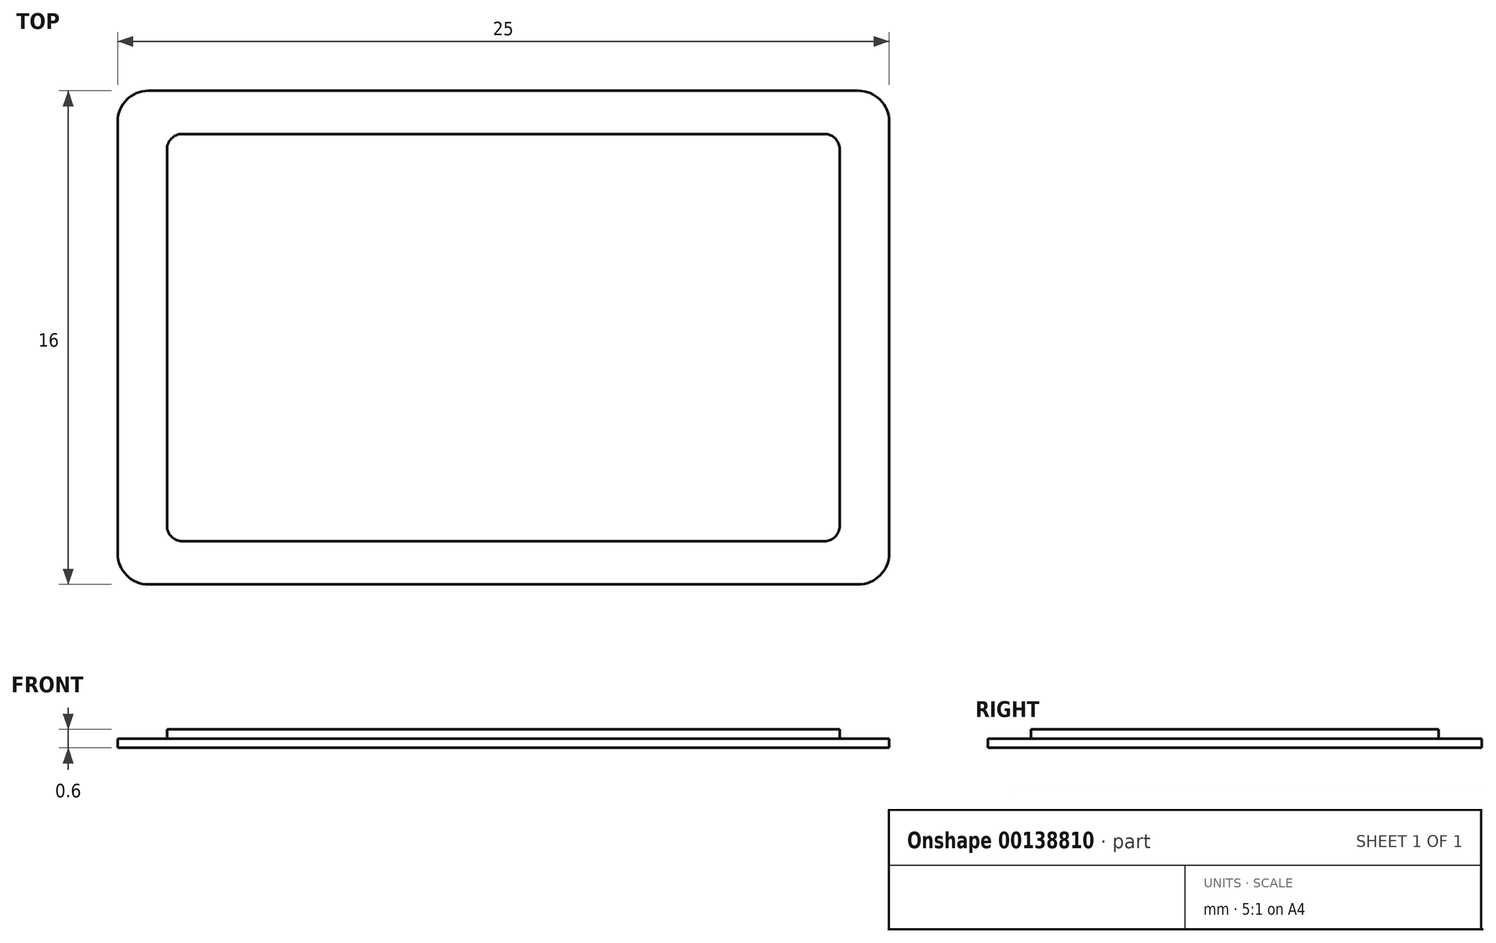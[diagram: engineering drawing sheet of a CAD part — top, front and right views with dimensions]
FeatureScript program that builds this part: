
annotation { "Feature Type Name" : "Feature", "Feature Type Description" : "" }
export const myFeature = defineFeature(function(context is Context, id is Id, definition is map)
    precondition{}
    {
        {
            var Q0;
            Q0=qCreatedBy(makeId("Top.planeOp"),FACE);
            var sketch = newSketch(context, id + "F0", { "sketchPlane" : qUnion([Q0])});
            skLineSegment(sketch, "E0.bottom", {"start": v(12.5, 8) * mm, "end": v(-12.5, 8) * mm});
            skLineSegment(sketch, "E0.top", {"start": v(12.5, -8) * mm, "end": v(-12.5, -8) * mm});
            skLineSegment(sketch, "E0.left", {"start": v(12.5, 8) * mm, "end": v(12.5, -8) * mm});
            skLineSegment(sketch, "E0.right", {"start": v(-12.5, 8) * mm, "end": v(-12.5, -8) * mm});
            skPoint(sketch, "E0.middle", {"position": v(0, 0) * mm});
            skLineSegment(sketch, "E1.bottom", {"start": v(10.9, 6.6) * mm, "end": v(-10.9, 6.6) * mm});
            skLineSegment(sketch, "E1.top", {"start": v(10.9, -6.6) * mm, "end": v(-10.9, -6.6) * mm});
            skLineSegment(sketch, "E1.left", {"start": v(10.9, 6.6) * mm, "end": v(10.9, -6.6) * mm});
            skLineSegment(sketch, "E1.right", {"start": v(-10.9, 6.6) * mm, "end": v(-10.9, -6.6) * mm});
            skSolve(sketch);
        }
        {
            var Q0;
            Q0=makeQuery(id+"F0.imprint","IMPRINT",FACE,{"disambiguationData":[TD([[makeQuery(id+"F0.imprint","IMPRINT",EDGE,{"derivedFrom":sQuery(id+"F0.wireOp",EDGE,"E1.bottom")}),1.0]])]});
            var Q1;
            Q1=makeQuery(id+"F0.imprint","IMPRINT",FACE,{"disambiguationData":[TD([[makeQuery(id+"F0.imprint","IMPRINT",EDGE,{"derivedFrom":sQuery(id+"F0.wireOp",EDGE,"E0.bottom")}),1.0]])]});
            extrude(context, id + "F1", {"entities" : qUnion([Q0, Q1]), "depth" : 0.3 * mm});
        }
        {
            var Q0;
            Q0=makeQuery(id+"F0.imprint","IMPRINT",FACE,{"disambiguationData":[TD([[makeQuery(id+"F0.imprint","IMPRINT",EDGE,{"derivedFrom":sQuery(id+"F0.wireOp",EDGE,"E1.bottom")}),1.0]])]});
            extrude(context, id + "F2", {"entities" : qUnion([Q0]), "operationType" : NewBodyOperationType.ADD, "depth" : 0.6 * mm});
        }
        {
            var Q0;
            Q0=makeQuery(id+"F1.opExtrude","SWEPT_EDGE",EDGE,{"disambiguationData":[OSD([sQuery(id+"F0.wireOp",EDGE,"E0.bottom"),sQuery(id+"F0.wireOp",EDGE,"E0.right")])]});
            var Q1;
            Q1=makeQuery(id+"F1.opExtrude","SWEPT_EDGE",EDGE,{"disambiguationData":[OSD([sQuery(id+"F0.wireOp",EDGE,"E0.top"),sQuery(id+"F0.wireOp",EDGE,"E0.right")])]});
            var Q2;
            Q2=makeQuery(id+"F1.opExtrude","SWEPT_EDGE",EDGE,{"disambiguationData":[OSD([sQuery(id+"F0.wireOp",EDGE,"E0.top"),sQuery(id+"F0.wireOp",EDGE,"E0.left")])]});
            var Q3;
            Q3=makeQuery(id+"F1.opExtrude","SWEPT_EDGE",EDGE,{"disambiguationData":[OSD([sQuery(id+"F0.wireOp",EDGE,"E0.bottom"),sQuery(id+"F0.wireOp",EDGE,"E0.left")])]});
            fillet(context, id + "F3", {"entities" : qUnion([Q0, Q1, Q2, Q3]), "radius" : 1 * mm, "allowEdgeOverflow" : false});
        }
        {
            var Q0;
            Q0=makeQuery(id+"F2.opExtrude","SWEPT_EDGE",EDGE,{"disambiguationData":[OSD([sQuery(id+"F0.wireOp",EDGE,"E1.top"),sQuery(id+"F0.wireOp",EDGE,"E1.right")])]});
            var Q1;
            Q1=makeQuery(id+"F2.opExtrude","SWEPT_EDGE",EDGE,{"disambiguationData":[OSD([sQuery(id+"F0.wireOp",EDGE,"E1.top"),sQuery(id+"F0.wireOp",EDGE,"E1.left")])]});
            var Q2;
            Q2=makeQuery(id+"F2.opExtrude","SWEPT_EDGE",EDGE,{"disambiguationData":[OSD([sQuery(id+"F0.wireOp",EDGE,"E1.bottom"),sQuery(id+"F0.wireOp",EDGE,"E1.right")])]});
            var Q3;
            Q3=makeQuery(id+"F2.opExtrude","SWEPT_EDGE",EDGE,{"disambiguationData":[OSD([sQuery(id+"F0.wireOp",EDGE,"E1.bottom"),sQuery(id+"F0.wireOp",EDGE,"E1.left")])]});
            fillet(context, id + "F4", {"entities" : qUnion([Q0, Q1, Q2, Q3]), "radius" : 0.5 * mm, "allowEdgeOverflow" : false});
        }
    });
